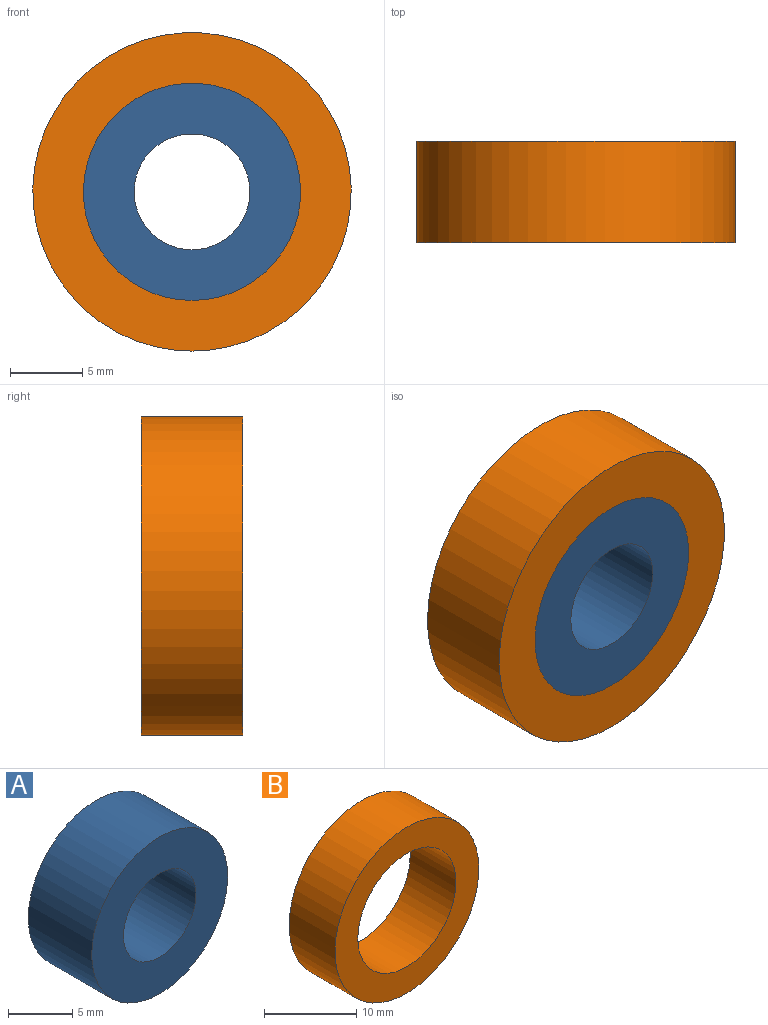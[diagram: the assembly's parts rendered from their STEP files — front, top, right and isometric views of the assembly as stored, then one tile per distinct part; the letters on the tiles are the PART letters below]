
ASSEMBLY  parts=2 mates=1
PART A: 4 faces, bbox 15x7x15 mm
  f0: cylinder r=4mm len=8mm, axis (0,1,0), area 175.9mm2, adj f2,f3
  f1: cylinder r=7.5mm len=15mm, axis (0,1,0), area 329.9mm2, adj f2,f3
  f2: plane 15x15mm, normal (0,-1,0), area 126.4mm2, adj f0,f1
  f3: plane 15x15mm, normal (0,1,0), area 126.4mm2, adj f0,f1
PART B: 4 faces, bbox 22x7x22 mm
  f0: cylinder r=7.5mm len=15mm, axis (0,1,0), area 329.9mm2, adj f2,f3
  f1: cylinder r=11mm len=22mm, axis (0,1,0), area 483.8mm2, adj f2,f3
  f2: plane 22x22mm, normal (0,-1,0), area 203.4mm2, adj f0,f1
  f3: plane 22x22mm, normal (0,1,0), area 203.4mm2, adj f0,f1
PLACE A at identity
PLACE B at identity fixed
MATE revolute A.f0 <-> B.f0  axis (0,1,0) through (0,0,0)mm
